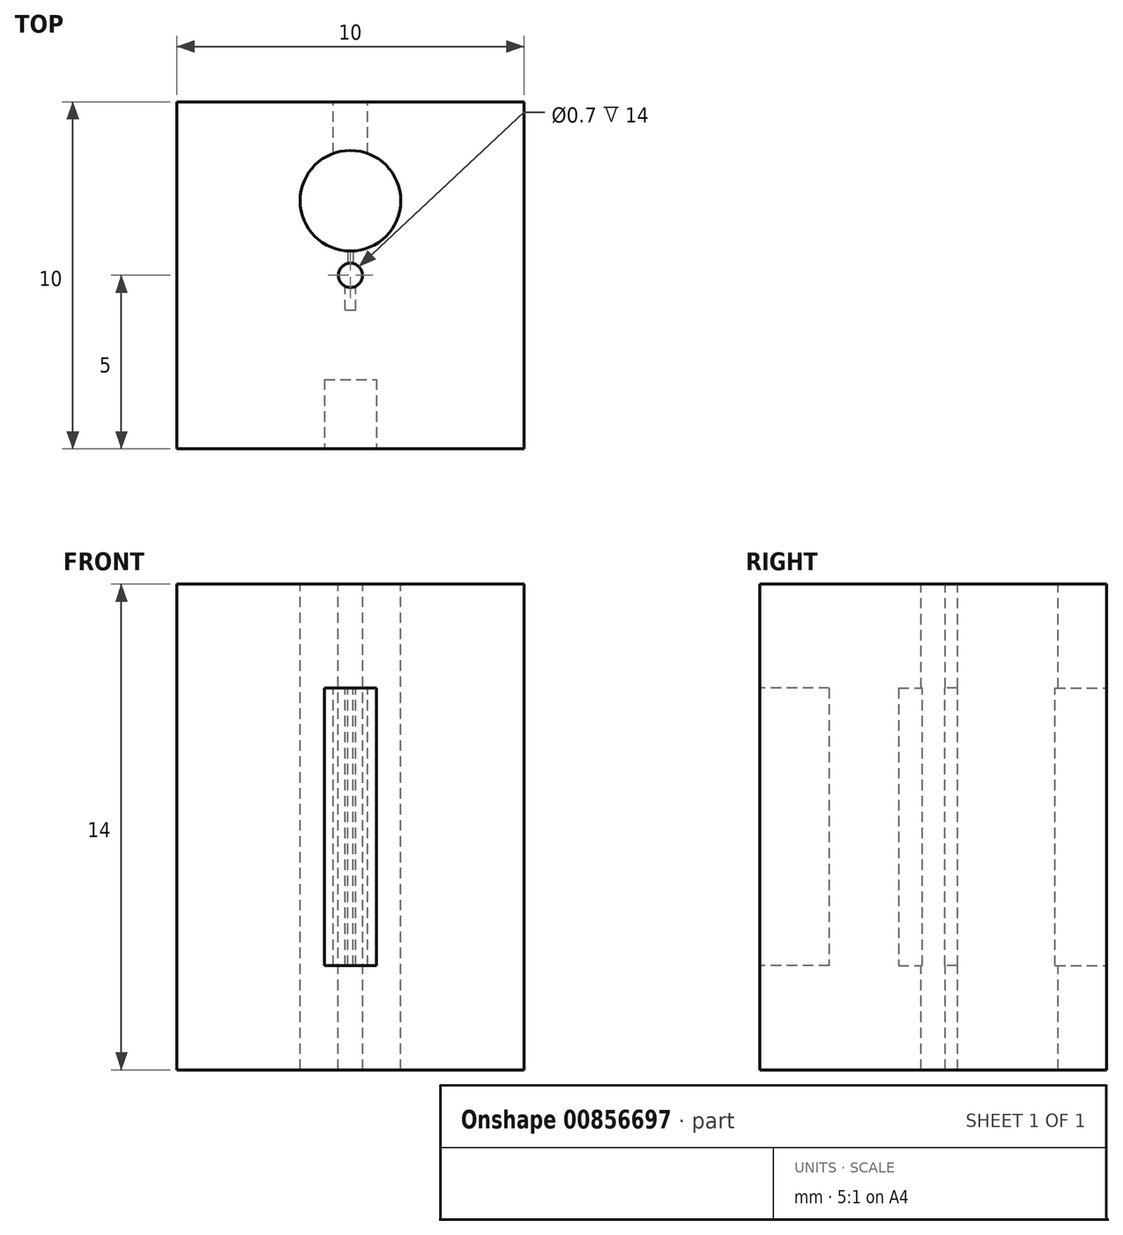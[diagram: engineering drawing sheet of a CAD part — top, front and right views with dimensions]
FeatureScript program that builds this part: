
annotation { "Feature Type Name" : "Feature", "Feature Type Description" : "" }
export const myFeature = defineFeature(function(context is Context, id is Id, definition is map)
    precondition{}
    {
        {
            var Q0;
            Q0=qCreatedBy(makeId("Top.planeOp"),FACE);
            var sketch = newSketch(context, id + "F0", { "sketchPlane" : qUnion([Q0])});
            skLineSegment(sketch, "E0.bottom", {"start": v(-5, 5) * mm, "end": v(5, 5) * mm});
            skLineSegment(sketch, "E0.top", {"start": v(-5, -5) * mm, "end": v(5, -5) * mm});
            skLineSegment(sketch, "E0.left", {"start": v(-5, 5) * mm, "end": v(-5, -5) * mm});
            skLineSegment(sketch, "E0.right", {"start": v(5, 5) * mm, "end": v(5, -5) * mm});
            skPoint(sketch, "E0.middle", {"position": v(0, 0) * mm});
            skSolve(sketch);
        }
        {
            var Q0;
            Q0=makeQuery(id+"F0.imprint","IMPRINT",FACE,{"disambiguationData":[TD([[makeQuery(id+"F0.imprint","IMPRINT",EDGE,{"derivedFrom":sQuery(id+"F0.wireOp",EDGE,"E0.bottom")}),-1.0]])]});
            extrude(context, id + "F1", {"entities" : qUnion([Q0]), "depth" : 14 * mm, "offsetDistance" : 25 * mm});
        }
        {
            var Q0;
            Q0=makeQuery(id+"F1.opExtrude","CAP_FACE",FACE,{"disambiguationData":[OSD([sQuery(id+"F0.wireOp",EDGE,"E0.bottom"),sQuery(id+"F0.wireOp",EDGE,"E0.top"),sQuery(id+"F0.wireOp",EDGE,"E0.left"),sQuery(id+"F0.wireOp",EDGE,"E0.right")])],"isStart":false});
            var sketch = newSketch(context, id + "F2", { "sketchPlane" : qUnion([Q0])});
            skCircle(sketch, "E1", {"center": v(0, 0) * mm, "radius": 0.35 * mm});
            skSolve(sketch);
        }
        {
            var Q0;
            Q0=qSketchRegion(id+"F2",true);
            extrude(context, id + "F3", {"entities" : qUnion([Q0]), "operationType" : NewBodyOperationType.REMOVE, "oppositeDirection" : true, "depth" : 14 * mm, "offsetDistance" : 25 * mm});
        }
        {
            var Q0;
            Q0=makeQuery(id+"F1.opExtrude","CAP_FACE",FACE,{"disambiguationData":[OSD([sQuery(id+"F0.wireOp",EDGE,"E0.bottom"),sQuery(id+"F0.wireOp",EDGE,"E0.top"),sQuery(id+"F0.wireOp",EDGE,"E0.left"),sQuery(id+"F0.wireOp",EDGE,"E0.right")])],"isStart":false});
            var sketch = newSketch(context, id + "F4", { "sketchPlane" : qUnion([Q0])});
            skCircle(sketch, "E2", {"center": v(0, 2.15) * mm, "radius": 1.45 * mm});
            skSolve(sketch);
        }
        {
            var Q0;
            Q0=qSketchRegion(id+"F4",true);
            extrude(context, id + "F5", {"entities" : qUnion([Q0]), "operationType" : NewBodyOperationType.REMOVE, "oppositeDirection" : true, "depth" : 14 * mm, "offsetDistance" : 25 * mm});
        }
        {
            var Q0;
            Q0=makeQuery(id+"F1.opExtrude","SWEPT_FACE",FACE,{"disambiguationData":[OSD([sQuery(id+"F0.wireOp",EDGE,"E0.bottom")])]});
            var sketch = newSketch(context, id + "F6", { "sketchPlane" : qUnion([Q0])});
            skLineSegment(sketch, "E3.bottom", {"start": v(0.5, 3) * mm, "end": v(-0.5, 3) * mm});
            skLineSegment(sketch, "E3.top", {"start": v(0.5, 11) * mm, "end": v(-0.5, 11) * mm});
            skLineSegment(sketch, "E3.left", {"start": v(0.5, 3) * mm, "end": v(0.5, 11) * mm});
            skLineSegment(sketch, "E3.right", {"start": v(-0.5, 3) * mm, "end": v(-0.5, 11) * mm});
            skPoint(sketch, "E3.middle", {"position": v(0, 7) * mm});
            skSolve(sketch);
        }
        {
            var Q0;
            Q0=qSketchRegion(id+"F6",true);
            extrude(context, id + "F7", {"entities" : qUnion([Q0]), "operationType" : NewBodyOperationType.REMOVE, "oppositeDirection" : true, "depth" : 2 * mm, "offsetDistance" : 25 * mm});
        }
        {
            var Q0;
            Q0=qCreatedBy(makeId("Front.planeOp"),FACE);
            var sketch = newSketch(context, id + "F8", { "sketchPlane" : qUnion([Q0])});
            skLineSegment(sketch, "E4.bottom", {"start": v(-0.08, 3) * mm, "end": v(0.07, 3) * mm});
            skLineSegment(sketch, "E4.top", {"start": v(-0.08, 11) * mm, "end": v(0.07, 11) * mm});
            skLineSegment(sketch, "E4.left", {"start": v(-0.08, 3) * mm, "end": v(-0.08, 11) * mm});
            skLineSegment(sketch, "E4.right", {"start": v(0.07, 3) * mm, "end": v(0.07, 11) * mm});
            skPoint(sketch, "E4.middle", {"position": v(0, 7) * mm});
            skSolve(sketch);
        }
        {
            var Q0;
            Q0=qSketchRegion(id+"F8",true);
            extrude(context, id + "F9", {"entities" : qUnion([Q0]), "operationType" : NewBodyOperationType.REMOVE, "oppositeDirection" : true, "depth" : 1 * mm, "offsetDistance" : 25 * mm});
        }
        {
            var Q0;
            Q0=qCreatedBy(makeId("Front.planeOp"),FACE);
            var sketch = newSketch(context, id + "F10", { "sketchPlane" : qUnion([Q0])});
            skLineSegment(sketch, "E5.bottom", {"start": v(-0.15, 11) * mm, "end": v(0.15, 11) * mm});
            skLineSegment(sketch, "E5.top", {"start": v(-0.15, 3) * mm, "end": v(0.15, 3) * mm});
            skLineSegment(sketch, "E5.left", {"start": v(-0.15, 11) * mm, "end": v(-0.15, 3) * mm});
            skLineSegment(sketch, "E5.right", {"start": v(0.15, 11) * mm, "end": v(0.15, 3) * mm});
            skPoint(sketch, "E5.middle", {"position": v(0, 7) * mm});
            skSolve(sketch);
        }
        {
            var Q0;
            Q0=qSketchRegion(id+"F10",true);
            extrude(context, id + "F11", {"entities" : qUnion([Q0]), "operationType" : NewBodyOperationType.REMOVE, "depth" : 1 * mm, "offsetDistance" : 25 * mm});
        }
        {
            var Q0;
            Q0=makeQuery(id+"F1.opExtrude","SWEPT_FACE",FACE,{"disambiguationData":[OSD([sQuery(id+"F0.wireOp",EDGE,"E0.top")])]});
            var sketch = newSketch(context, id + "F12", { "sketchPlane" : qUnion([Q0])});
            skLineSegment(sketch, "E6.bottom", {"start": v(-0.75, 11) * mm, "end": v(0.75, 11) * mm});
            skLineSegment(sketch, "E6.top", {"start": v(-0.75, 3) * mm, "end": v(0.75, 3) * mm});
            skLineSegment(sketch, "E6.left", {"start": v(-0.75, 11) * mm, "end": v(-0.75, 3) * mm});
            skLineSegment(sketch, "E6.right", {"start": v(0.75, 11) * mm, "end": v(0.75, 3) * mm});
            skPoint(sketch, "E6.middle", {"position": v(0, 7) * mm});
            skSolve(sketch);
        }
        {
            var Q0;
            Q0=qSketchRegion(id+"F12",true);
            extrude(context, id + "F13", {"entities" : qUnion([Q0]), "operationType" : NewBodyOperationType.REMOVE, "oppositeDirection" : true, "depth" : 2 * mm, "offsetDistance" : 25 * mm});
        }
    });
